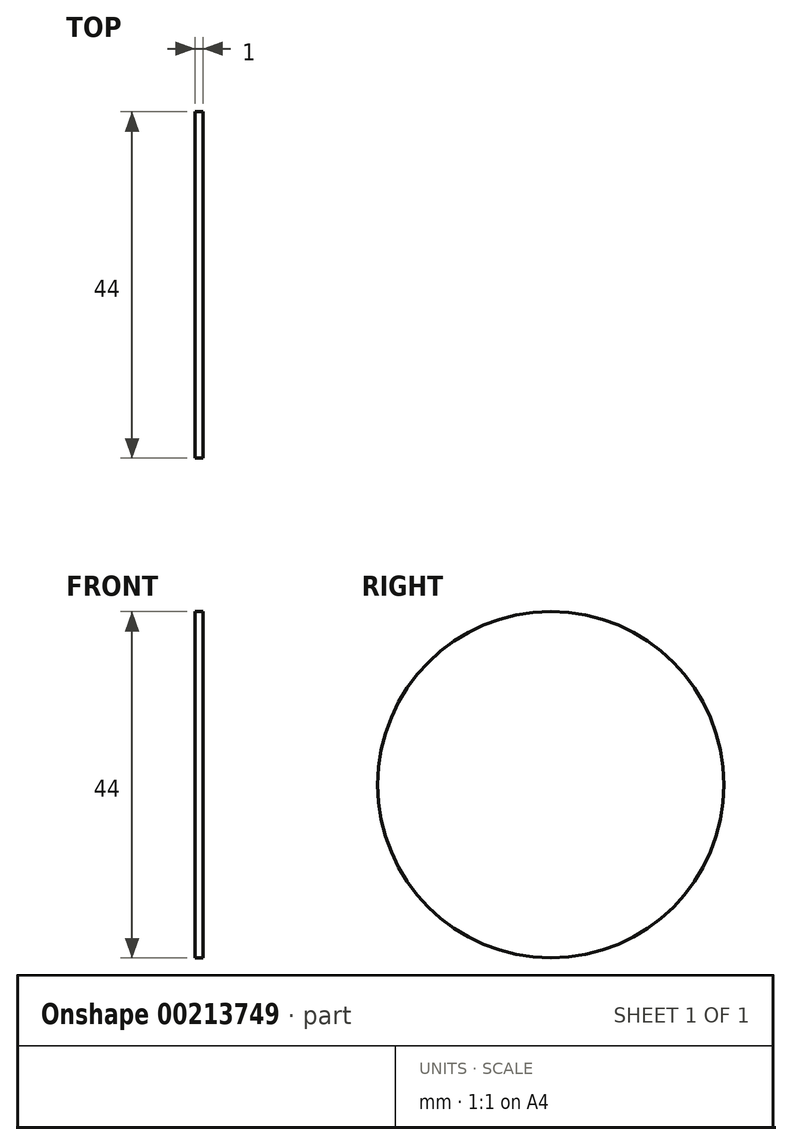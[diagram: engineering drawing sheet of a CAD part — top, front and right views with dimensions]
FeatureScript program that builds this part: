
annotation { "Feature Type Name" : "Feature", "Feature Type Description" : "" }
export const myFeature = defineFeature(function(context is Context, id is Id, definition is map)
    precondition{}
    {
        {
            var Q0;
            Q0=qCreatedBy(makeId("Right.planeOp"),FACE);
            var sketch = newSketch(context, id + "F0", { "sketchPlane" : qUnion([Q0])});
            skCircle(sketch, "E0", {"center": v(0, 0) * mm, "radius": 22 * mm});
            skSolve(sketch);
        }
        {
            var Q0;
            Q0=makeQuery(id+"F0.imprint","IMPRINT",FACE,{"disambiguationData":[TD([[makeQuery(id+"F0.imprint","IMPRINT",EDGE,{"derivedFrom":sQuery(id+"F0.wireOp",EDGE,"E0")}),1.0]])]});
            extrude(context, id + "F1", {"entities" : qUnion([Q0]), "depth" : 1 * mm});
        }
    });
